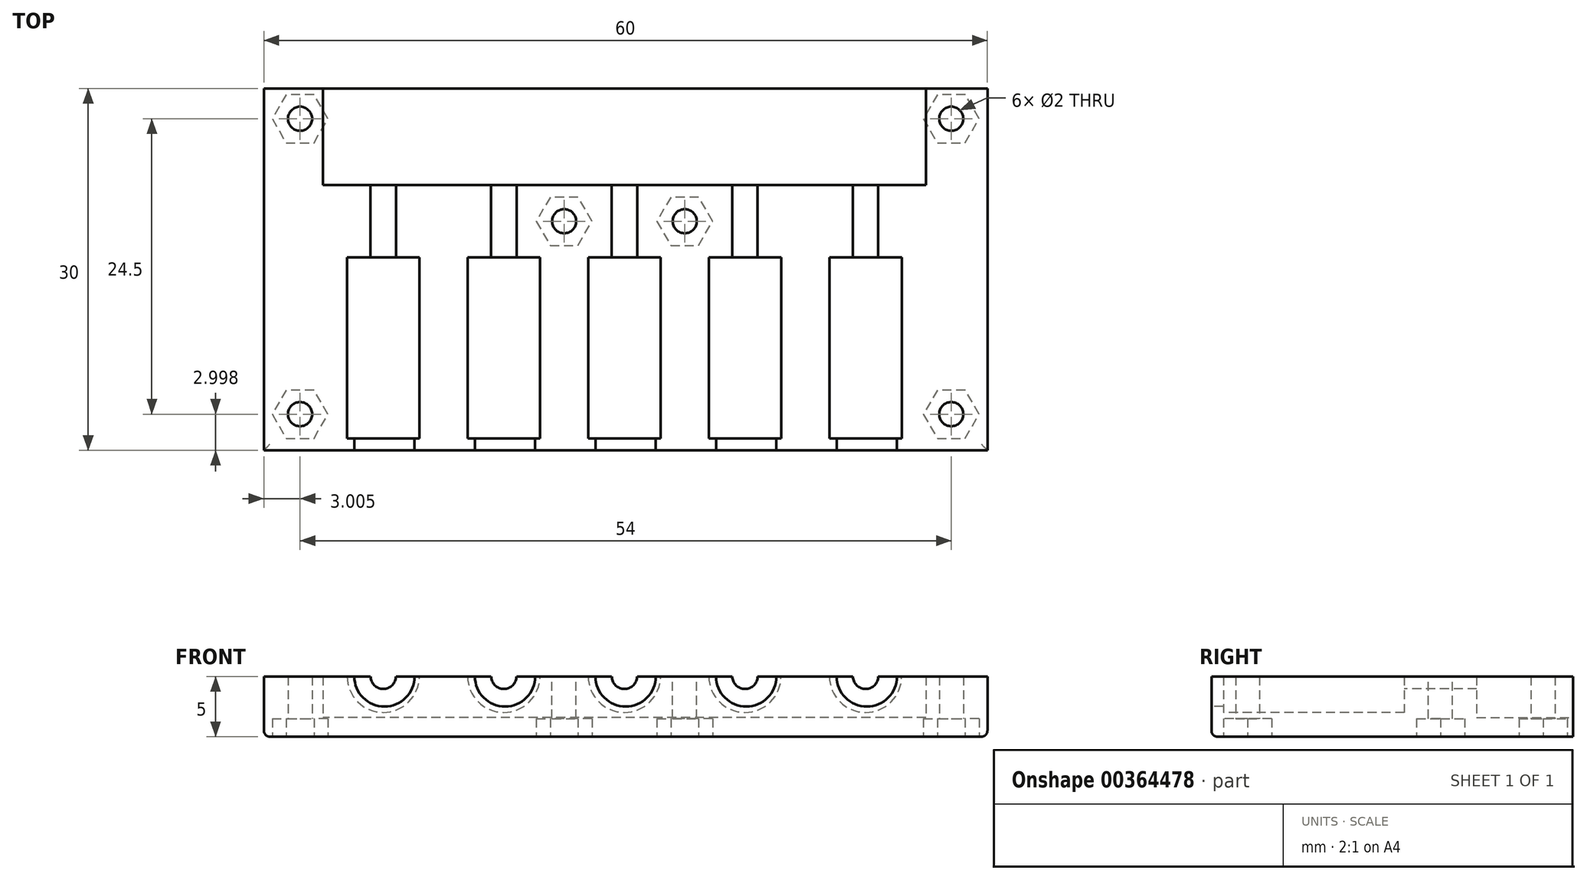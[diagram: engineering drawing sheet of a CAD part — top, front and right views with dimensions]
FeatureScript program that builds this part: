
annotation { "Feature Type Name" : "Feature", "Feature Type Description" : "" }
export const myFeature = defineFeature(function(context is Context, id is Id, definition is map)
    precondition{}
    {
        {
            var Q0;
            Q0=qCreatedBy(makeId("Top.planeOp"),FACE);
            var sketch = newSketch(context, id + "F0", { "sketchPlane" : qUnion([Q0])});
            skLineSegment(sketch, "E0.bottom", {"start": v(-32.95, 5.2) * mm, "end": v(27.05, 5.2) * mm});
            skLineSegment(sketch, "E0.top", {"start": v(-32.95, -19.8) * mm, "end": v(27.05, -19.8) * mm});
            skLineSegment(sketch, "E0.left", {"start": v(-32.95, 5.2) * mm, "end": v(-32.95, -19.8) * mm});
            skLineSegment(sketch, "E0.right", {"start": v(27.05, 5.2) * mm, "end": v(27.05, -19.8) * mm});
            skSolve(sketch);
        }
        {
            var Q0;
            Q0=qSketchRegion(id+"F0",true);
            extrude(context, id + "F1", {"entities" : qUnion([Q0]), "depth" : 5 * mm});
        }
        {
            var Q0;
            Q0=makeQuery(id+"F1.opExtrude","SWEPT_FACE",FACE,{"disambiguationData":[OSD([sQuery(id+"F0.wireOp",EDGE,"E0.top")])]});
            var sketch = newSketch(context, id + "F2", { "sketchPlane" : qUnion([Q0])});
            skCircle(sketch, "E1", {"center": v(-22.95, 5) * mm, "radius": 2.5 * mm});
            skCircle(sketch, "E2.1.0.0", {"center": v(-12.95, 5) * mm, "radius": 2.5 * mm});
            skCircle(sketch, "E2.2.0.0", {"center": v(-2.95, 5) * mm, "radius": 2.5 * mm});
            skCircle(sketch, "E2.3.0.0", {"center": v(7.05, 5) * mm, "radius": 2.5 * mm});
            skCircle(sketch, "E2.4.0.0", {"center": v(17.05, 5) * mm, "radius": 2.5 * mm});
            skLineSegment(sketch, "E2.direction1", {"start": v(-22.95, 5) * mm, "end": v(-12.95, 5) * mm, "construction": true});
            skSolve(sketch);
        }
        {
            var Q0;
            Q0=qSketchRegion(id+"F2",true);
            extrude(context, id + "F3", {"entities" : qUnion([Q0]), "operationType" : NewBodyOperationType.REMOVE, "oppositeDirection" : true, "depth" : 10 * mm});
        }
        {
            var Q0;
            Q0=makeQuery(id+"F1.opExtrude","SWEPT_FACE",FACE,{"disambiguationData":[OSD([sQuery(id+"F0.wireOp",EDGE,"E0.top")])]});
            cPlane(context, id + "F4", {"entities" : qUnion([Q0]), "cplaneType" : CPlaneType.OFFSET, "offset" : 1 * mm, "oppositeDirection" : true, "width" : 150 * mm, "height" : 150 * mm});
        }
        {
            var Q0;
            Q0=qCreatedBy(id+"F4.planeOp",FACE);
            var sketch = newSketch(context, id + "F5", { "sketchPlane" : qUnion([Q0])});
            skCircle(sketch, "E3", {"center": v(-23.05, 5.01) * mm, "radius": 3 * mm});
            skCircle(sketch, "E4.1.0.0", {"center": v(-13.05, 5.01) * mm, "radius": 3 * mm});
            skCircle(sketch, "E4.2.0.0", {"center": v(-3.05, 5.01) * mm, "radius": 3 * mm});
            skCircle(sketch, "E4.3.0.0", {"center": v(6.95, 5.01) * mm, "radius": 3 * mm});
            skCircle(sketch, "E4.4.0.0", {"center": v(16.95, 5.01) * mm, "radius": 3 * mm});
            skLineSegment(sketch, "E4.direction1", {"start": v(-23.05, 5.01) * mm, "end": v(-13.05, 5.01) * mm, "construction": true});
            skSolve(sketch);
        }
        {
            var Q0;
            Q0=qSketchRegion(id+"F5",true);
            extrude(context, id + "F6", {"entities" : qUnion([Q0]), "operationType" : NewBodyOperationType.REMOVE, "oppositeDirection" : true, "depth" : 15 * mm});
        }
        {
            var Q0;
            Q0=makeQuery(id+"F6.boolean.opBoolean","COPY",FACE,{"derivedFrom":makeQuery(id+"F6.opExtrude","CAP_FACE",FACE,{"disambiguationData":[OSD([sQuery(id+"F5.wireOp",EDGE,"E3")])],"isStart":false})});
            var sketch = newSketch(context, id + "F7", { "sketchPlane" : qUnion([Q0])});
            skCircle(sketch, "E5", {"center": v(-23.05, 5.01) * mm, "radius": 1.05 * mm});
            skCircle(sketch, "E6.1.0.0", {"center": v(-13.05, 5.01) * mm, "radius": 1.05 * mm});
            skCircle(sketch, "E6.2.0.0", {"center": v(-3.05, 5.01) * mm, "radius": 1.05 * mm});
            skCircle(sketch, "E6.3.0.0", {"center": v(6.95, 5.01) * mm, "radius": 1.05 * mm});
            skCircle(sketch, "E6.4.0.0", {"center": v(16.95, 5.01) * mm, "radius": 1.05 * mm});
            skLineSegment(sketch, "E6.direction1", {"start": v(-23.05, 5.01) * mm, "end": v(-13.05, 5.01) * mm, "construction": true});
            skSolve(sketch);
        }
        {
            var Q0;
            Q0=qSketchRegion(id+"F7",true);
            extrude(context, id + "F8", {"entities" : qUnion([Q0]), "operationType" : NewBodyOperationType.REMOVE, "oppositeDirection" : true, "depth" : 29 * mm});
        }
        {
            var Q0;
            Q0=makeQuery(id+"F1.opExtrude","SWEPT_FACE",FACE,{"disambiguationData":[OSD([sQuery(id+"F0.wireOp",EDGE,"E0.bottom")])]});
            var sketch = newSketch(context, id + "F9", { "sketchPlane" : qUnion([Q0])});
            skLineSegment(sketch, "E7.bottom", {"start": v(-21.95, 5) * mm, "end": v(28.05, 5) * mm});
            skLineSegment(sketch, "E7.top", {"start": v(-21.95, 1.58) * mm, "end": v(28.05, 1.58) * mm});
            skLineSegment(sketch, "E7.left", {"start": v(-21.95, 5) * mm, "end": v(-21.95, 1.58) * mm});
            skLineSegment(sketch, "E7.right", {"start": v(28.05, 5) * mm, "end": v(28.05, 1.58) * mm});
            skSolve(sketch);
        }
        {
            var Q0;
            Q0=qSketchRegion(id+"F9",true);
            extrude(context, id + "F10", {"entities" : qUnion([Q0]), "operationType" : NewBodyOperationType.REMOVE, "oppositeDirection" : true, "depth" : 3 * mm});
        }
        {
            var Q0;
            Q0=makeQuery(id+"F1.opExtrude","SWEPT_FACE",FACE,{"disambiguationData":[OSD([sQuery(id+"F0.wireOp",EDGE,"E0.bottom")])]});
            extrude(context, id + "F11", {"entities" : qUnion([Q0]), "operationType" : NewBodyOperationType.ADD, "depth" : 5 * mm});
        }
        {
            var Q0;
            {var subQ0=sQuery(id+"F0.wireOp",EDGE,"E0.right");var subQ1=sQuery(id+"F0.wireOp",EDGE,"E0.bottom");Q0=makeQuery(id+"F11.boolean.opBoolean","MERGE",EDGE,{"derivedFrom":[makeQuery(id+"F1.opExtrude","CAP_EDGE",EDGE,{"disambiguationData":[OSD([subQ0])],"isStart":true}),makeQuery(id+"F11.opExtrude","SWEPT_EDGE",EDGE,{"disambiguationData":[OSD([subQ1,subQ0]),TDD([makeQuery(id+"F1.opExtrude","CAP_VERTEX",VERTEX,{"disambiguationData":[OSD([subQ1,subQ0])],"isStart":true})])]})]});}
            var Q1;
            Q1=makeQuery(id+"F1.opExtrude","CAP_EDGE",EDGE,{"disambiguationData":[OSD([sQuery(id+"F0.wireOp",EDGE,"E0.top")])],"isStart":true});
            var Q2;
            Q2=makeQuery(id+"FEIolAkUxVgGt6m_1.opLoft","SWEPT_EDGE",EDGE,{"disambiguationData":[OSD([sQuery(id+"F0.wireOp",EDGE,"E0.bottom"),sQuery(id+"F0.wireOp",EDGE,"E0.right"),sQuery(id+"F4cxA0SiljIs9s8_1.wireOp",EDGE,"Jk4UEFDV-4BQ6-7r7a-iLyf-OHepFeUpgrdx.top"),sQuery(id+"F4cxA0SiljIs9s8_1.wireOp",EDGE,"Jk4UEFDV-4BQ6-7r7a-iLyf-OHepFeUpgrdx.left")])]});
            var Q3;
            Q3=makeQuery(id+"FEIolAkUxVgGt6m_1.opLoft","MID_CAP_EDGE",EDGE,{"disambiguationData":[OSD([sQuery(id+"F4cxA0SiljIs9s8_1.wireOp",EDGE,"Jk4UEFDV-4BQ6-7r7a-iLyf-OHepFeUpgrdx.top"),sQuery(id+"F4cxA0SiljIs9s8_1.wireOp",EDGE,"Jk4UEFDV-4BQ6-7r7a-iLyf-OHepFeUpgrdx.left"),sQuery(id+"F4cxA0SiljIs9s8_1.wireOp",EDGE,"Jk4UEFDV-4BQ6-7r7a-iLyf-OHepFeUpgrdx.right")])],"capPos":1.0});
            var Q4;
            Q4=makeQuery(id+"FEIolAkUxVgGt6m_1.opLoft","SWEPT_EDGE",EDGE,{"disambiguationData":[OSD([sQuery(id+"F0.wireOp",EDGE,"E0.bottom"),sQuery(id+"F0.wireOp",EDGE,"E0.left"),sQuery(id+"F4cxA0SiljIs9s8_1.wireOp",EDGE,"Jk4UEFDV-4BQ6-7r7a-iLyf-OHepFeUpgrdx.top"),sQuery(id+"F4cxA0SiljIs9s8_1.wireOp",EDGE,"Jk4UEFDV-4BQ6-7r7a-iLyf-OHepFeUpgrdx.right")])]});
            var Q5;
            {var subQ0=sQuery(id+"F0.wireOp",EDGE,"E0.left");var subQ1=sQuery(id+"F0.wireOp",EDGE,"E0.bottom");Q5=makeQuery(id+"F11.boolean.opBoolean","MERGE",EDGE,{"derivedFrom":[makeQuery(id+"F1.opExtrude","CAP_EDGE",EDGE,{"disambiguationData":[OSD([subQ0])],"isStart":true}),makeQuery(id+"F11.opExtrude","SWEPT_EDGE",EDGE,{"disambiguationData":[OSD([subQ1,subQ0]),TDD([makeQuery(id+"F1.opExtrude","CAP_VERTEX",VERTEX,{"disambiguationData":[OSD([subQ1,subQ0])],"isStart":true})])]})]});}
            fillet(context, id + "F12", {"entities" : qUnion([Q0, Q1, Q2, Q3, Q4, Q5]), "radius" : 0.5 * mm, "tangentPropagation" : true, "allowEdgeOverflow" : false});
        }
        {
            var Q0;
            {var subQ0=sQuery(id+"F0.wireOp",EDGE,"E0.bottom");Q0=makeQuery(id+"F11.boolean.opBoolean","MERGE",FACE,{"derivedFrom":[makeQuery(id+"F1.opExtrude","CAP_FACE",FACE,{"disambiguationData":[OSD([subQ0,sQuery(id+"F0.wireOp",EDGE,"E0.top"),sQuery(id+"F0.wireOp",EDGE,"E0.left"),sQuery(id+"F0.wireOp",EDGE,"E0.right")])],"isStart":true}),makeQuery(id+"F11.opExtrude","SWEPT_FACE",FACE,{"disambiguationData":[OSD([subQ0]),TDD([makeQuery(id+"F1.opExtrude","CAP_EDGE",EDGE,{"disambiguationData":[OSD([subQ0])],"isStart":true})])]})]});}
            var sketch = newSketch(context, id + "F13", { "sketchPlane" : qUnion([Q0])});
            skLineSegment(sketch, "E8", {"start": v(-2.95, 19.3) * mm, "end": v(-2.95, -10.2) * mm});
            skCircle(sketch, "E9", {"center": v(-29.95, 16.8) * mm, "radius": 1 * mm});
            skCircle(sketch, "E10.MirrorC", {"center": v(24.05, 16.8) * mm, "radius": 1 * mm});
            skSolve(sketch);
        }
        {
            var Q0;
            {var subQ7=sQuery(id+"F13.wireOp",EDGE,"E8");Q0=makeQuery(id+"F13.imprint","IMPRINT",FACE,{"disambiguationData":[TD([[makeQuery(id+"F13.imprint","IMPRINT",EDGE,{"derivedFrom":subQ7}),-1.0]])]});}
            var sketch = newSketch(context, id + "F14", { "sketchPlane" : qUnion([Q0])});
            skCircle(sketch, "E11", {"center": v(-29.95, -7.7) * mm, "radius": 1 * mm});
            skCircle(sketch, "E12.MirrorC", {"center": v(24.05, -7.7) * mm, "radius": 1 * mm});
            skSolve(sketch);
        }
        {
            var Q0;
            Q0=qSketchRegion(id+"F14",true);
            var Q1;
            Q1=qSketchRegion(id+"F13",true);
            extrude(context, id + "F15", {"entities" : qUnion([Q0, Q1]), "operationType" : NewBodyOperationType.REMOVE, "endBound" : BoundingType.THROUGH_ALL, "oppositeDirection" : true, "depth" : 25 * mm});
        }
        {
            var Q0;
            {var subQ0=sQuery(id+"F5.wireOp",EDGE,"E4.4.0.0");var subQ1=sQuery(id+"F0.wireOp",EDGE,"E0.top");var subQ2=sQuery(id+"F5.wireOp",EDGE,"E4.3.0.0");var subQ3=sQuery(id+"F0.wireOp",EDGE,"E0.bottom");Q0=makeQuery(id+"F8.boolean.opBoolean","SPLIT",FACE,{"disambiguationData":[TD([makeQuery(id+"F1.opExtrude","SWEPT_FACE",FACE,{"disambiguationData":[OSD([subQ3])]}),makeQuery(id+"F1.opExtrude","SWEPT_FACE",FACE,{"disambiguationData":[OSD([subQ1])]}),makeQuery(id+"F3.boolean.opBoolean","COPY",FACE,{"derivedFrom":makeQuery(id+"F3.opExtrude","SWEPT_FACE",FACE,{"disambiguationData":[OSD([sQuery(id+"F2.wireOp",EDGE,"E2.3.0.0")])]})}),makeQuery(id+"F3.boolean.opBoolean","COPY",FACE,{"derivedFrom":makeQuery(id+"F3.opExtrude","SWEPT_FACE",FACE,{"disambiguationData":[OSD([sQuery(id+"F2.wireOp",EDGE,"E2.4.0.0")])]})}),makeQuery(id+"F6.boolean.opBoolean","COPY",FACE,{"derivedFrom":makeQuery(id+"F6.opExtrude","SWEPT_FACE",FACE,{"disambiguationData":[OSD([subQ2])]})}),makeQuery(id+"F6.boolean.opBoolean","COPY",FACE,{"derivedFrom":makeQuery(id+"F6.opExtrude","CAP_FACE",FACE,{"disambiguationData":[OSD([subQ2])],"isStart":true})}),makeQuery(id+"F6.boolean.opBoolean","COPY",FACE,{"derivedFrom":makeQuery(id+"F6.opExtrude","CAP_FACE",FACE,{"disambiguationData":[OSD([subQ2])],"isStart":false})}),makeQuery(id+"F6.boolean.opBoolean","COPY",FACE,{"derivedFrom":makeQuery(id+"F6.opExtrude","SWEPT_FACE",FACE,{"disambiguationData":[OSD([subQ0])]})}),makeQuery(id+"F6.boolean.opBoolean","COPY",FACE,{"derivedFrom":makeQuery(id+"F6.opExtrude","CAP_FACE",FACE,{"disambiguationData":[OSD([subQ0])],"isStart":true})}),makeQuery(id+"F6.boolean.opBoolean","COPY",FACE,{"derivedFrom":makeQuery(id+"F6.opExtrude","CAP_FACE",FACE,{"disambiguationData":[OSD([subQ0])],"isStart":false})}),makeQuery(id+"F8.opExtrude","SWEPT_FACE",FACE,{"disambiguationData":[OSD([sQuery(id+"F7.wireOp",EDGE,"E6.3.0.0")])]}),makeQuery(id+"F8.opExtrude","SWEPT_FACE",FACE,{"disambiguationData":[OSD([sQuery(id+"F7.wireOp",EDGE,"E6.4.0.0")])]})])],"derivedFrom":makeQuery(id+"F1.opExtrude","CAP_FACE",FACE,{"disambiguationData":[OSD([subQ3,subQ1,sQuery(id+"F0.wireOp",EDGE,"E0.left"),sQuery(id+"F0.wireOp",EDGE,"E0.right")])],"isStart":false})});}
            var sketch = newSketch(context, id + "F16", { "sketchPlane" : qUnion([Q0])});
            skCircle(sketch, "E13", {"center": v(1.95, -0.8) * mm, "radius": 1 * mm});
            skCircle(sketch, "E14.1.0.0", {"center": v(-8.05, -0.8) * mm, "radius": 1 * mm});
            skLineSegment(sketch, "E14.direction1", {"start": v(1.95, -0.8) * mm, "end": v(-8.05, -0.8) * mm, "construction": true});
            skSolve(sketch);
        }
        {
            var Q0;
            Q0=qSketchRegion(id+"F16",true);
            extrude(context, id + "F17", {"entities" : qUnion([Q0]), "operationType" : NewBodyOperationType.REMOVE, "oppositeDirection" : true, "depth" : 5 * mm});
        }
        {
            var Q0;
            {var subQ0=sQuery(id+"F0.wireOp",EDGE,"E0.bottom");Q0=makeQuery(id+"F11.boolean.opBoolean","MERGE",FACE,{"derivedFrom":[makeQuery(id+"F1.opExtrude","CAP_FACE",FACE,{"disambiguationData":[OSD([subQ0,sQuery(id+"F0.wireOp",EDGE,"E0.top"),sQuery(id+"F0.wireOp",EDGE,"E0.left"),sQuery(id+"F0.wireOp",EDGE,"E0.right")])],"isStart":true}),makeQuery(id+"F11.opExtrude","SWEPT_FACE",FACE,{"disambiguationData":[OSD([subQ0]),TDD([makeQuery(id+"F1.opExtrude","CAP_EDGE",EDGE,{"disambiguationData":[OSD([subQ0])],"isStart":true})])]})]});}
            var sketch = newSketch(context, id + "F18", { "sketchPlane" : qUnion([Q0])});
            skCircle(sketch, "E15.cCircle", {"center": v(24.05, -7.7) * mm, "radius": 2 * mm, "construction": true});
            skLineSegment(sketch, "E15.0", {"start": v(22.9, -5.7) * mm, "end": v(25.2, -5.7) * mm});
            skLineSegment(sketch, "E15.1", {"start": v(25.2, -5.7) * mm, "end": v(26.36, -7.7) * mm});
            skLineSegment(sketch, "E15.2", {"start": v(26.36, -7.7) * mm, "end": v(25.2, -9.7) * mm});
            skLineSegment(sketch, "E15.3", {"start": v(25.2, -9.7) * mm, "end": v(22.9, -9.7) * mm});
            skLineSegment(sketch, "E15.4", {"start": v(22.9, -9.7) * mm, "end": v(21.75, -7.7) * mm});
            skLineSegment(sketch, "E15.5", {"start": v(21.75, -7.7) * mm, "end": v(22.9, -5.7) * mm});
            skPoint(sketch, "E15.0.midPoint", {"position": v(24.05, -5.7) * mm});
            skCircle(sketch, "E16.cCircle", {"center": v(24.05, 16.8) * mm, "radius": 2 * mm, "construction": true});
            skLineSegment(sketch, "E16.0", {"start": v(22.9, 18.8) * mm, "end": v(25.2, 18.8) * mm});
            skLineSegment(sketch, "E16.1", {"start": v(25.2, 18.8) * mm, "end": v(26.36, 16.8) * mm});
            skLineSegment(sketch, "E16.2", {"start": v(26.36, 16.8) * mm, "end": v(25.2, 14.8) * mm});
            skLineSegment(sketch, "E16.3", {"start": v(25.2, 14.8) * mm, "end": v(22.9, 14.8) * mm});
            skLineSegment(sketch, "E16.4", {"start": v(22.9, 14.8) * mm, "end": v(21.75, 16.8) * mm});
            skLineSegment(sketch, "E16.5", {"start": v(21.75, 16.8) * mm, "end": v(22.9, 18.8) * mm});
            skPoint(sketch, "E16.0.midPoint", {"position": v(24.05, 18.8) * mm});
            skCircle(sketch, "E17.cCircle", {"center": v(-29.95, 16.8) * mm, "radius": 2 * mm, "construction": true});
            skLineSegment(sketch, "E17.0", {"start": v(-31.1, 18.8) * mm, "end": v(-28.8, 18.8) * mm});
            skLineSegment(sketch, "E17.1", {"start": v(-28.8, 18.8) * mm, "end": v(-27.64, 16.8) * mm});
            skLineSegment(sketch, "E17.2", {"start": v(-27.64, 16.8) * mm, "end": v(-28.8, 14.8) * mm});
            skLineSegment(sketch, "E17.3", {"start": v(-28.8, 14.8) * mm, "end": v(-31.1, 14.8) * mm});
            skLineSegment(sketch, "E17.4", {"start": v(-31.1, 14.8) * mm, "end": v(-32.25, 16.8) * mm});
            skLineSegment(sketch, "E17.5", {"start": v(-32.25, 16.8) * mm, "end": v(-31.1, 18.8) * mm});
            skPoint(sketch, "E17.0.midPoint", {"position": v(-29.95, 18.8) * mm});
            skCircle(sketch, "E18.cCircle", {"center": v(-29.95, -7.7) * mm, "radius": 2 * mm, "construction": true});
            skLineSegment(sketch, "E18.0", {"start": v(-28.8, -9.7) * mm, "end": v(-31.1, -9.7) * mm});
            skLineSegment(sketch, "E18.1", {"start": v(-31.1, -9.7) * mm, "end": v(-32.25, -7.7) * mm});
            skLineSegment(sketch, "E18.2", {"start": v(-32.25, -7.7) * mm, "end": v(-31.1, -5.7) * mm});
            skLineSegment(sketch, "E18.3", {"start": v(-31.1, -5.7) * mm, "end": v(-28.8, -5.7) * mm});
            skLineSegment(sketch, "E18.4", {"start": v(-28.8, -5.7) * mm, "end": v(-27.64, -7.7) * mm});
            skLineSegment(sketch, "E18.5", {"start": v(-27.64, -7.7) * mm, "end": v(-28.8, -9.7) * mm});
            skPoint(sketch, "E18.0.midPoint", {"position": v(-29.95, -9.7) * mm});
            skCircle(sketch, "E19.cCircle", {"center": v(1.95, 0.8) * mm, "radius": 2 * mm, "construction": true});
            skLineSegment(sketch, "E19.0", {"start": v(3.1, -1.2) * mm, "end": v(0.8, -1.2) * mm});
            skLineSegment(sketch, "E19.1", {"start": v(0.8, -1.2) * mm, "end": v(-0.36, 0.8) * mm});
            skLineSegment(sketch, "E19.2", {"start": v(-0.36, 0.8) * mm, "end": v(0.8, 2.8) * mm});
            skLineSegment(sketch, "E19.3", {"start": v(0.8, 2.8) * mm, "end": v(3.1, 2.8) * mm});
            skLineSegment(sketch, "E19.4", {"start": v(3.1, 2.8) * mm, "end": v(4.26, 0.8) * mm});
            skLineSegment(sketch, "E19.5", {"start": v(4.26, 0.8) * mm, "end": v(3.1, -1.2) * mm});
            skPoint(sketch, "E19.0.midPoint", {"position": v(1.95, -1.2) * mm});
            skCircle(sketch, "E20.cCircle", {"center": v(-8.05, 0.8) * mm, "radius": 2 * mm, "construction": true});
            skLineSegment(sketch, "E20.0", {"start": v(-6.9, -1.2) * mm, "end": v(-9.2, -1.2) * mm});
            skLineSegment(sketch, "E20.1", {"start": v(-9.2, -1.2) * mm, "end": v(-10.36, 0.8) * mm});
            skLineSegment(sketch, "E20.2", {"start": v(-10.36, 0.8) * mm, "end": v(-9.2, 2.8) * mm});
            skLineSegment(sketch, "E20.3", {"start": v(-9.2, 2.8) * mm, "end": v(-6.9, 2.8) * mm});
            skLineSegment(sketch, "E20.4", {"start": v(-6.9, 2.8) * mm, "end": v(-5.74, 0.8) * mm});
            skLineSegment(sketch, "E20.5", {"start": v(-5.74, 0.8) * mm, "end": v(-6.9, -1.2) * mm});
            skPoint(sketch, "E20.0.midPoint", {"position": v(-8.05, -1.2) * mm});
            skSolve(sketch);
        }
        {
            var Q0;
            Q0 = qSketchRegion(id + "F18", true);
            extrude(context, id + "F19", {"entities" : qUnion([Q0]), "operationType" : NewBodyOperationType.REMOVE, "oppositeDirection" : true, "depth" : 1.5 * mm});
        }
    });
